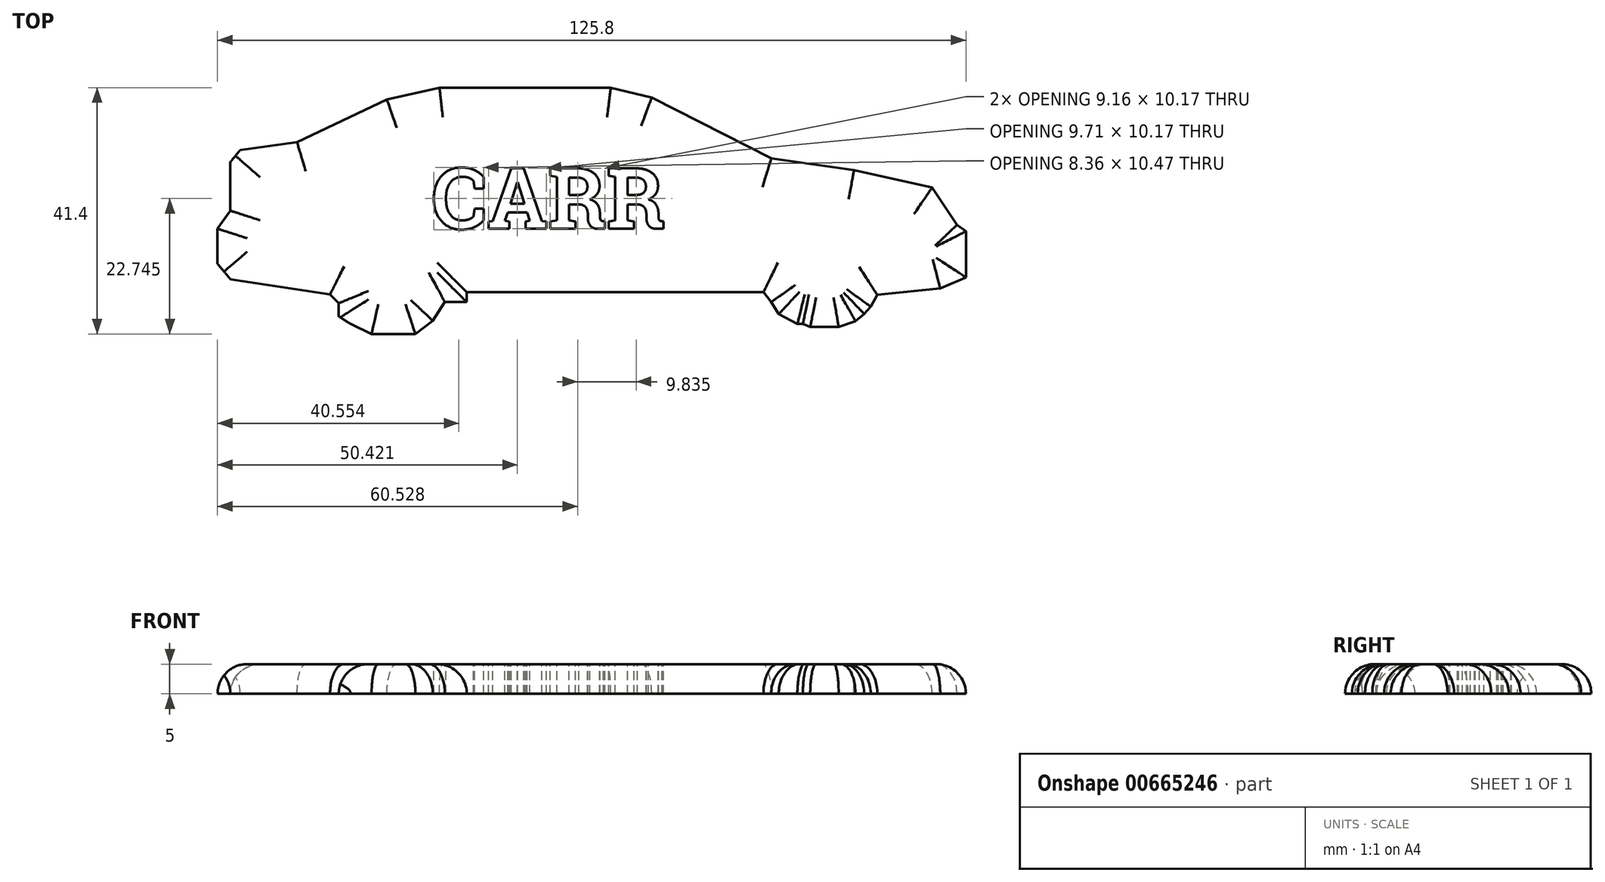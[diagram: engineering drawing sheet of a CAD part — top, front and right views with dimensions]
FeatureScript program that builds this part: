
annotation { "Feature Type Name" : "Feature", "Feature Type Description" : "" }
export const myFeature = defineFeature(function(context is Context, id is Id, definition is map)
    precondition{}
    {
        {
            var Q0;
            Q0=qCreatedBy(makeId("Top.planeOp"),FACE);
            var sketch = newSketch(context, id + "F0", { "sketchPlane" : qUnion([Q0])});
            skLineSegment(sketch, "E0", {"start": v(-33.03, 5.06) * mm, "end": v(-41.86, 3.04) * mm});
            skLineSegment(sketch, "E1", {"start": v(-41.86, 3.04) * mm, "end": v(-56.95, -4.14) * mm});
            skLineSegment(sketch, "E2", {"start": v(-56.95, -4.14) * mm, "end": v(-66.51, -5.43) * mm});
            skLineSegment(sketch, "E3", {"start": v(-66.51, -5.43) * mm, "end": v(-68.17, -7.45) * mm});
            skLineSegment(sketch, "E4", {"start": v(-68.17, -7.45) * mm, "end": v(-68.17, -11.13) * mm});
            skLineSegment(sketch, "E5", {"start": v(-68.17, -11.13) * mm, "end": v(-68.17, -15.64) * mm});
            skPoint(sketch, "E5.endSnap0", {"position": v(-70.33, -15.64) * mm});
            skLineSegment(sketch, "E6", {"start": v(-68.17, -15.64) * mm, "end": v(-70.33, -18.68) * mm});
            skLineSegment(sketch, "E7", {"start": v(-70.33, -18.68) * mm, "end": v(-70.33, -24.56) * mm});
            skLineSegment(sketch, "E8", {"start": v(-70.33, -24.56) * mm, "end": v(-68.17, -27.14) * mm});
            skLineSegment(sketch, "E9", {"start": v(-68.17, -27.14) * mm, "end": v(-51.43, -29.72) * mm});
            skLineSegment(sketch, "E10", {"start": v(-51.43, -29.72) * mm, "end": v(-49.95, -31.19) * mm});
            skLineSegment(sketch, "E11", {"start": v(-49.95, -31.19) * mm, "end": v(-49.95, -33.4) * mm});
            skLineSegment(sketch, "E12", {"start": v(-49.95, -33.4) * mm, "end": v(-47.93, -34.68) * mm});
            skLineSegment(sketch, "E13", {"start": v(-47.93, -34.68) * mm, "end": v(-44.43, -36.34) * mm});
            skLineSegment(sketch, "E14", {"start": v(-44.43, -36.34) * mm, "end": v(-41.3, -36.34) * mm});
            skLineSegment(sketch, "E15", {"start": v(-41.3, -36.34) * mm, "end": v(-37.08, -36.34) * mm});
            skLineSegment(sketch, "E16", {"start": v(-37.08, -36.34) * mm, "end": v(-34.13, -34.13) * mm});
            skLineSegment(sketch, "E17", {"start": v(-34.13, -34.13) * mm, "end": v(-32.1, -31) * mm});
            skLineSegment(sketch, "E18", {"start": v(-32.1, -31) * mm, "end": v(-28.43, -31) * mm});
            skLineSegment(sketch, "E19", {"start": v(-28.43, -31) * mm, "end": v(-28.43, -29.35) * mm});
            skLineSegment(sketch, "E20", {"start": v(-28.43, -29.35) * mm, "end": v(21.44, -29.35) * mm});
            skLineSegment(sketch, "E21", {"start": v(21.44, -29.35) * mm, "end": v(22.72, -31) * mm});
            skLineSegment(sketch, "E22", {"start": v(22.72, -31) * mm, "end": v(24.01, -33.03) * mm});
            skLineSegment(sketch, "E23", {"start": v(24.01, -33.03) * mm, "end": v(27.14, -34.68) * mm});
            skLineSegment(sketch, "E24", {"start": v(27.14, -34.68) * mm, "end": v(28.07, -34.68) * mm});
            skLineSegment(sketch, "E25", {"start": v(-33.03, 5.06) * mm, "end": v(-27.44, 5.06) * mm});
            skLineSegment(sketch, "E26", {"start": v(-27.44, 5.06) * mm, "end": v(-9.51, 5.06) * mm});
            skLineSegment(sketch, "E27", {"start": v(-9.51, 5.06) * mm, "end": v(-4.23, 5.06) * mm});
            skLineSegment(sketch, "E28", {"start": v(-4.23, 5.06) * mm, "end": v(2.65, 3.36) * mm});
            skLineSegment(sketch, "E29", {"start": v(2.65, 3.36) * mm, "end": v(22.79, -6.83) * mm});
            skLineSegment(sketch, "E30", {"start": v(22.79, -6.83) * mm, "end": v(36.67, -8.8) * mm});
            skLineSegment(sketch, "E31", {"start": v(36.67, -8.8) * mm, "end": v(49.8, -11.74) * mm});
            skLineSegment(sketch, "E32", {"start": v(49.8, -11.74) * mm, "end": v(53.98, -18) * mm});
            skLineSegment(sketch, "E33", {"start": v(53.98, -18) * mm, "end": v(55.47, -19.1) * mm});
            skLineSegment(sketch, "E34", {"start": v(55.47, -19.1) * mm, "end": v(55.47, -26.84) * mm});
            skLineSegment(sketch, "E35", {"start": v(55.47, -26.84) * mm, "end": v(51.16, -28.69) * mm});
            skLineSegment(sketch, "E36", {"start": v(51.16, -28.69) * mm, "end": v(40.6, -29.8) * mm});
            skLineSegment(sketch, "E37", {"start": v(40.6, -29.8) * mm, "end": v(39.49, -31.76) * mm});
            skLineSegment(sketch, "E38", {"start": v(39.49, -31.76) * mm, "end": v(38.38, -32.98) * mm});
            skLineSegment(sketch, "E39", {"start": v(38.38, -32.98) * mm, "end": v(36.91, -34.21) * mm});
            skLineSegment(sketch, "E40", {"start": v(36.91, -34.21) * mm, "end": v(34.09, -35.2) * mm});
            skLineSegment(sketch, "E41", {"start": v(34.09, -35.2) * mm, "end": v(31.5, -35.2) * mm});
            skLineSegment(sketch, "E42", {"start": v(31.5, -35.2) * mm, "end": v(29.3, -35.2) * mm});
            skLineSegment(sketch, "E43", {"start": v(29.3, -35.2) * mm, "end": v(28.07, -34.68) * mm});
            skSolve(sketch);
        }
        {
            var Q0;
            Q0 = qSketchRegion(id + "F0", true);
            extrude(context, id + "F1", {"entities" : qUnion([Q0]), "depth" : 5 * mm, "offsetDistance" : 25 * mm});
        }
        {
            var Q0;
            Q0=makeQuery(id+"F1.opExtrude","CAP_FACE",FACE,{"disambiguationData":[OSD([sQuery(id+"F0.wireOp",EDGE,"E0"),sQuery(id+"F0.wireOp",EDGE,"E1"),sQuery(id+"F0.wireOp",EDGE,"E2"),sQuery(id+"F0.wireOp",EDGE,"E3"),sQuery(id+"F0.wireOp",EDGE,"E4"),sQuery(id+"F0.wireOp",EDGE,"E5"),sQuery(id+"F0.wireOp",EDGE,"E6"),sQuery(id+"F0.wireOp",EDGE,"E7"),sQuery(id+"F0.wireOp",EDGE,"E8"),sQuery(id+"F0.wireOp",EDGE,"E9"),sQuery(id+"F0.wireOp",EDGE,"E10"),sQuery(id+"F0.wireOp",EDGE,"E11"),sQuery(id+"F0.wireOp",EDGE,"E12"),sQuery(id+"F0.wireOp",EDGE,"E13"),sQuery(id+"F0.wireOp",EDGE,"E14"),sQuery(id+"F0.wireOp",EDGE,"E15"),sQuery(id+"F0.wireOp",EDGE,"E16"),sQuery(id+"F0.wireOp",EDGE,"E17"),sQuery(id+"F0.wireOp",EDGE,"E18"),sQuery(id+"F0.wireOp",EDGE,"E19"),sQuery(id+"F0.wireOp",EDGE,"E20"),sQuery(id+"F0.wireOp",EDGE,"E21"),sQuery(id+"F0.wireOp",EDGE,"E22"),sQuery(id+"F0.wireOp",EDGE,"E23"),sQuery(id+"F0.wireOp",EDGE,"E24"),sQuery(id+"F0.wireOp",EDGE,"E25"),sQuery(id+"F0.wireOp",EDGE,"E26"),sQuery(id+"F0.wireOp",EDGE,"E27"),sQuery(id+"F0.wireOp",EDGE,"E28"),sQuery(id+"F0.wireOp",EDGE,"E29"),sQuery(id+"F0.wireOp",EDGE,"E30"),sQuery(id+"F0.wireOp",EDGE,"E31"),sQuery(id+"F0.wireOp",EDGE,"E32"),sQuery(id+"F0.wireOp",EDGE,"E33"),sQuery(id+"F0.wireOp",EDGE,"E34"),sQuery(id+"F0.wireOp",EDGE,"E35"),sQuery(id+"F0.wireOp",EDGE,"E36"),sQuery(id+"F0.wireOp",EDGE,"E37"),sQuery(id+"F0.wireOp",EDGE,"E38"),sQuery(id+"F0.wireOp",EDGE,"E39"),sQuery(id+"F0.wireOp",EDGE,"E40"),sQuery(id+"F0.wireOp",EDGE,"E41"),sQuery(id+"F0.wireOp",EDGE,"E42"),sQuery(id+"F0.wireOp",EDGE,"E43")])],"isStart":false});
            fillet(context, id + "F2", {"entities" : qUnion([Q0]), "radius" : 5 * mm, "tangentPropagation" : true, "allowEdgeOverflow" : false});
        }
        {
            var Q0;
            Q0=makeQuery(id+"F1.opExtrude","CAP_FACE",FACE,{"disambiguationData":[OSD([sQuery(id+"F0.wireOp",EDGE,"E0"),sQuery(id+"F0.wireOp",EDGE,"E1"),sQuery(id+"F0.wireOp",EDGE,"E2"),sQuery(id+"F0.wireOp",EDGE,"E3"),sQuery(id+"F0.wireOp",EDGE,"E4"),sQuery(id+"F0.wireOp",EDGE,"E5"),sQuery(id+"F0.wireOp",EDGE,"E6"),sQuery(id+"F0.wireOp",EDGE,"E7"),sQuery(id+"F0.wireOp",EDGE,"E8"),sQuery(id+"F0.wireOp",EDGE,"E9"),sQuery(id+"F0.wireOp",EDGE,"E10"),sQuery(id+"F0.wireOp",EDGE,"E11"),sQuery(id+"F0.wireOp",EDGE,"E12"),sQuery(id+"F0.wireOp",EDGE,"E13"),sQuery(id+"F0.wireOp",EDGE,"E14"),sQuery(id+"F0.wireOp",EDGE,"E15"),sQuery(id+"F0.wireOp",EDGE,"E16"),sQuery(id+"F0.wireOp",EDGE,"E17"),sQuery(id+"F0.wireOp",EDGE,"E18"),sQuery(id+"F0.wireOp",EDGE,"E19"),sQuery(id+"F0.wireOp",EDGE,"E20"),sQuery(id+"F0.wireOp",EDGE,"E21"),sQuery(id+"F0.wireOp",EDGE,"E22"),sQuery(id+"F0.wireOp",EDGE,"E23"),sQuery(id+"F0.wireOp",EDGE,"E24"),sQuery(id+"F0.wireOp",EDGE,"E25"),sQuery(id+"F0.wireOp",EDGE,"E26"),sQuery(id+"F0.wireOp",EDGE,"E27"),sQuery(id+"F0.wireOp",EDGE,"E28"),sQuery(id+"F0.wireOp",EDGE,"E29"),sQuery(id+"F0.wireOp",EDGE,"E30"),sQuery(id+"F0.wireOp",EDGE,"E31"),sQuery(id+"F0.wireOp",EDGE,"E32"),sQuery(id+"F0.wireOp",EDGE,"E33"),sQuery(id+"F0.wireOp",EDGE,"E34"),sQuery(id+"F0.wireOp",EDGE,"E35"),sQuery(id+"F0.wireOp",EDGE,"E36"),sQuery(id+"F0.wireOp",EDGE,"E37"),sQuery(id+"F0.wireOp",EDGE,"E38"),sQuery(id+"F0.wireOp",EDGE,"E39"),sQuery(id+"F0.wireOp",EDGE,"E40"),sQuery(id+"F0.wireOp",EDGE,"E41"),sQuery(id+"F0.wireOp",EDGE,"E42"),sQuery(id+"F0.wireOp",EDGE,"E43")])],"isStart":false});
            var sketch = newSketch(context, id + "F3", { "sketchPlane" : qUnion([Q0])});
            skText(sketch, "E44", { "text": "CARR", "fontName": "RobotoSlab-Bold.ttf"});
            const initialGuessF3  = {"E44": [-0.03432, -0.01868, 1, 0, 0.0103]};
            skSetInitialGuess(sketch, initialGuessF3);
            skSolve(sketch);
        }
        {
            var Q0;
            Q0 = qSketchRegion(id + "F3", true);
            extrude(context, id + "F4", {"entities" : qUnion([Q0]), "operationType" : NewBodyOperationType.REMOVE, "oppositeDirection" : true, "depth" : 5 * mm, "offsetDistance" : 25 * mm});
        }
    });
